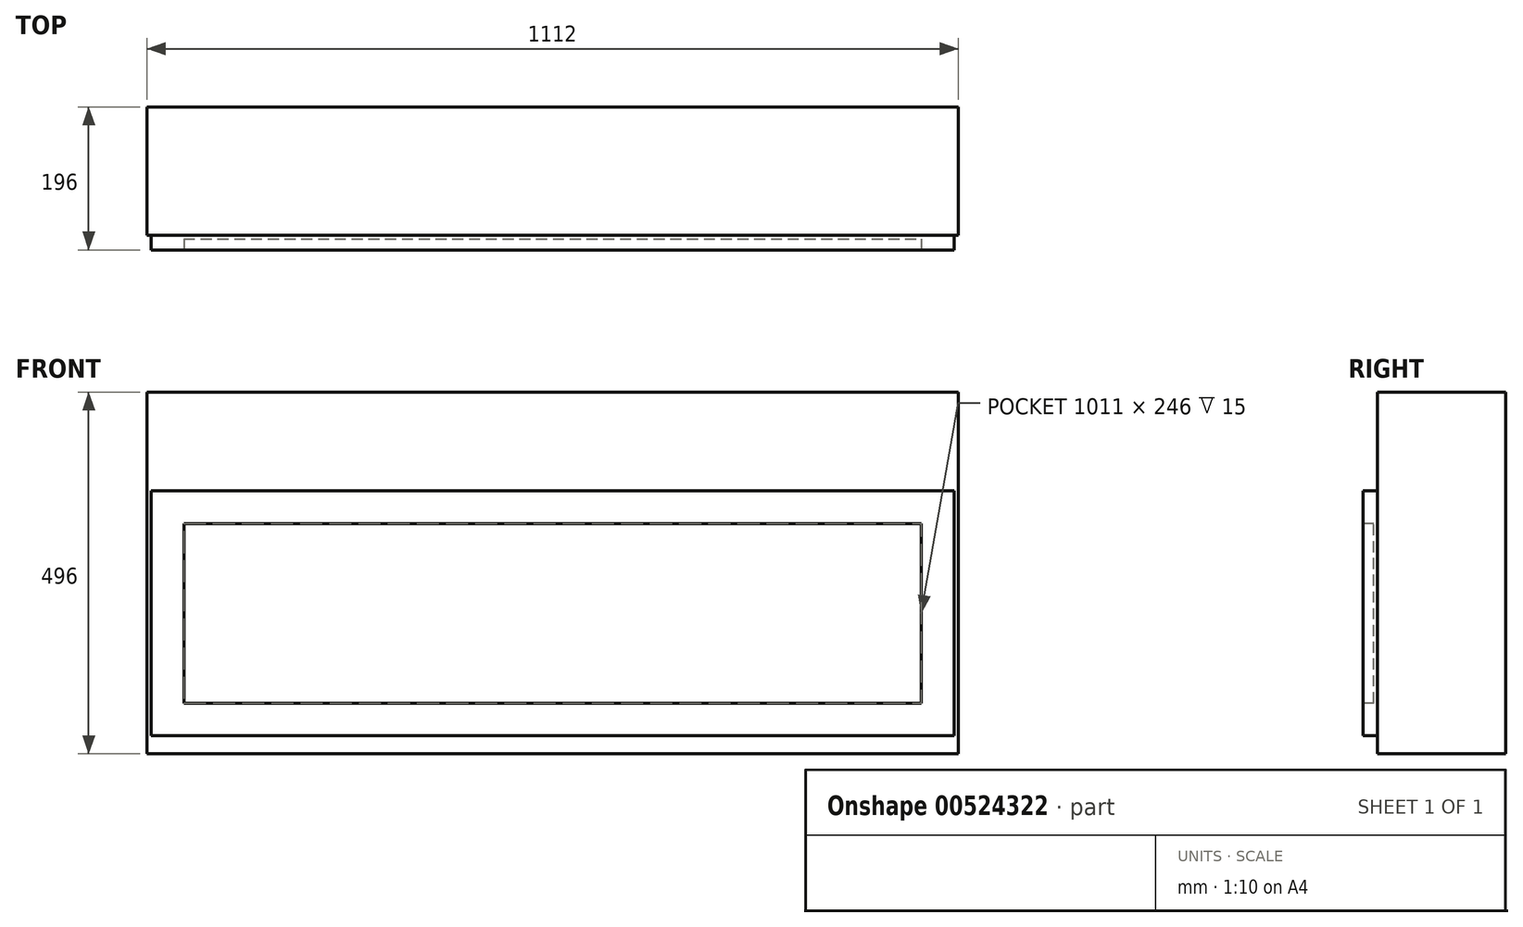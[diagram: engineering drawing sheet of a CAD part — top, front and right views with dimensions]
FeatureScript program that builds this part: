
annotation { "Feature Type Name" : "Feature", "Feature Type Description" : "" }
export const myFeature = defineFeature(function(context is Context, id is Id, definition is map)
    precondition{}
    {
        {
            var Q0;
            Q0=qCreatedBy(makeId("Front.planeOp"),FACE);
            var sketch = newSketch(context, id + "F0", { "sketchPlane" : qUnion([Q0])});
            skLineSegment(sketch, "E0.bottom", {"start": v(556, -248) * mm, "end": v(-556, -248) * mm});
            skLineSegment(sketch, "E0.top", {"start": v(556, 248) * mm, "end": v(-556, 248) * mm});
            skLineSegment(sketch, "E0.left", {"start": v(556, -248) * mm, "end": v(556, 248) * mm});
            skLineSegment(sketch, "E0.right", {"start": v(-556, -248) * mm, "end": v(-556, 248) * mm});
            skPoint(sketch, "E0.middle", {"position": v(0, 0) * mm});
            skSolve(sketch);
        }
        {
            var Q0;
            Q0 = qSketchRegion(id + "F0", true);
            extrude(context, id + "F1", {"entities" : qUnion([Q0]), "depth" : 176 * mm, "offsetDistance" : 25 * mm});
        }
        {
            var Q0;
            Q0=makeQuery(id+"F1.opExtrude","CAP_FACE",FACE,{"disambiguationData":[OSD([sQuery(id+"F0.wireOp",EDGE,"E0.bottom"),sQuery(id+"F0.wireOp",EDGE,"E0.top"),sQuery(id+"F0.wireOp",EDGE,"E0.left"),sQuery(id+"F0.wireOp",EDGE,"E0.right")])],"isStart":false});
            var sketch = newSketch(context, id + "F2", { "sketchPlane" : qUnion([Q0])});
            skLineSegment(sketch, "E1.bottom", {"start": v(550.5, -223.5) * mm, "end": v(-550.5, -223.5) * mm});
            skLineSegment(sketch, "E1.top", {"start": v(550.5, 112.5) * mm, "end": v(-550.5, 112.5) * mm});
            skLineSegment(sketch, "E1.left", {"start": v(550.5, -223.5) * mm, "end": v(550.5, 112.5) * mm});
            skLineSegment(sketch, "E1.right", {"start": v(-550.5, -223.5) * mm, "end": v(-550.5, 112.5) * mm});
            skPoint(sketch, "E1.middle", {"position": v(0, -55.5) * mm});
            skSolve(sketch);
        }
        {
            var Q0;
            Q0=makeQuery(id+"F2.imprint","IMPRINT",FACE,{"disambiguationData":[TD([[makeQuery(id+"F2.imprint","IMPRINT",EDGE,{"derivedFrom":sQuery(id+"F2.wireOp",EDGE,"E1.bottom")}),-1.0]])]});
            extrude(context, id + "F3", {"entities" : qUnion([Q0]), "operationType" : NewBodyOperationType.ADD, "depth" : 20 * mm, "offsetDistance" : 25 * mm});
        }
        {
            var Q0;
            Q0=makeQuery(id+"F3.opExtrude","CAP_FACE",FACE,{"disambiguationData":[OSD([sQuery(id+"F2.wireOp",EDGE,"E1.bottom"),sQuery(id+"F2.wireOp",EDGE,"E1.top"),sQuery(id+"F2.wireOp",EDGE,"E1.left"),sQuery(id+"F2.wireOp",EDGE,"E1.right")])],"isStart":false});
            var sketch = newSketch(context, id + "F4", { "sketchPlane" : qUnion([Q0])});
            skLineSegment(sketch, "E2.0", {"start": v(505.5, -178.5) * mm, "end": v(505.5, 67.5) * mm});
            skLineSegment(sketch, "E2.1", {"start": v(-505.5, -178.5) * mm, "end": v(505.5, -178.5) * mm});
            skLineSegment(sketch, "E2.2", {"start": v(-505.5, 67.5) * mm, "end": v(-505.5, -178.5) * mm});
            skLineSegment(sketch, "E2.3", {"start": v(505.5, 67.5) * mm, "end": v(-505.5, 67.5) * mm});
            skSolve(sketch);
        }
        {
            var Q0;
            Q0 = qSketchRegion(id + "F4", true);
            extrude(context, id + "F5", {"entities" : qUnion([Q0]), "operationType" : NewBodyOperationType.REMOVE, "oppositeDirection" : true, "depth" : 15 * mm, "offsetDistance" : 25 * mm});
        }
    });
